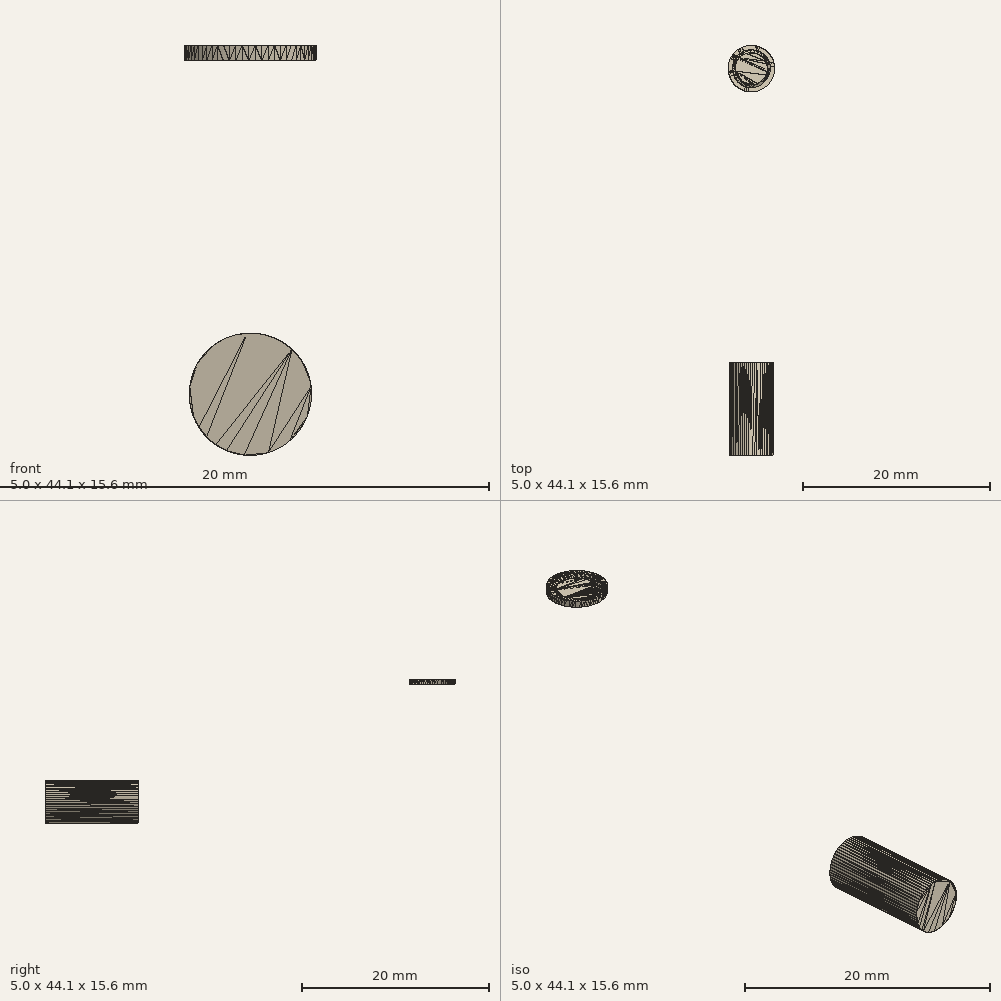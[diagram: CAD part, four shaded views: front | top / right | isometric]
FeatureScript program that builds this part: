
annotation { "Feature Type Name" : "Feature", "Feature Type Description" : "" }
export const myFeature = defineFeature(function(context is Context, id is Id, definition is map)
    precondition{}
    {
        {
            var Q0;
            Q0=qCreatedBy(makeId("Front.planeOp"),FACE);
            var sketch = newSketch(context, id + "F0", { "sketchPlane" : qUnion([Q0])});
            skCircle(sketch, "E0", {"center": v(0, 0) * mm, "radius": 2.33 * mm});
            skSolve(sketch);
        }
        {
            var Q0;
            Q0=qSketchRegion(id+"F0",true);
            extrude(context, id + "F1", {"entities" : qUnion([Q0]), "depth" : 10 * mm});
        }
        {
            var Q0;
            Q0=qCreatedBy(makeId("Right.planeOp"),FACE);
            var sketch = newSketch(context, id + "F2", { "sketchPlane" : qUnion([Q0])});
            skLineSegment(sketch, "E1", {"start": v(31.58, 12.68) * mm, "end": v(29.08, 12.68) * mm});
            skLineSegment(sketch, "E2", {"start": v(29.08, 12.68) * mm, "end": v(29.08, 13.26) * mm});
            skLineSegment(sketch, "E3", {"start": v(29.08, 13.26) * mm, "end": v(29.55, 13.26) * mm});
            skLineSegment(sketch, "E4", {"start": v(29.55, 13.26) * mm, "end": v(29.86, 12.98) * mm});
            skLineSegment(sketch, "E5", {"start": v(29.86, 12.98) * mm, "end": v(31.58, 12.98) * mm});
            skLineSegment(sketch, "E6", {"start": v(31.58, 12.98) * mm, "end": v(31.58, 12.68) * mm});
            skSolve(sketch);
        }
        {
            var Q0;
            Q0=qSketchRegion(id+"F2",true);
            var Q1;
            Q1=sQuery(id+"F2.wireOp",EDGE,"E6");
            revolve(context, id + "F3", {"entities" : qUnion([Q0]), "axis" : qUnion([Q1]), "revolveType" : RevolveType.FULL});
        }
    });
